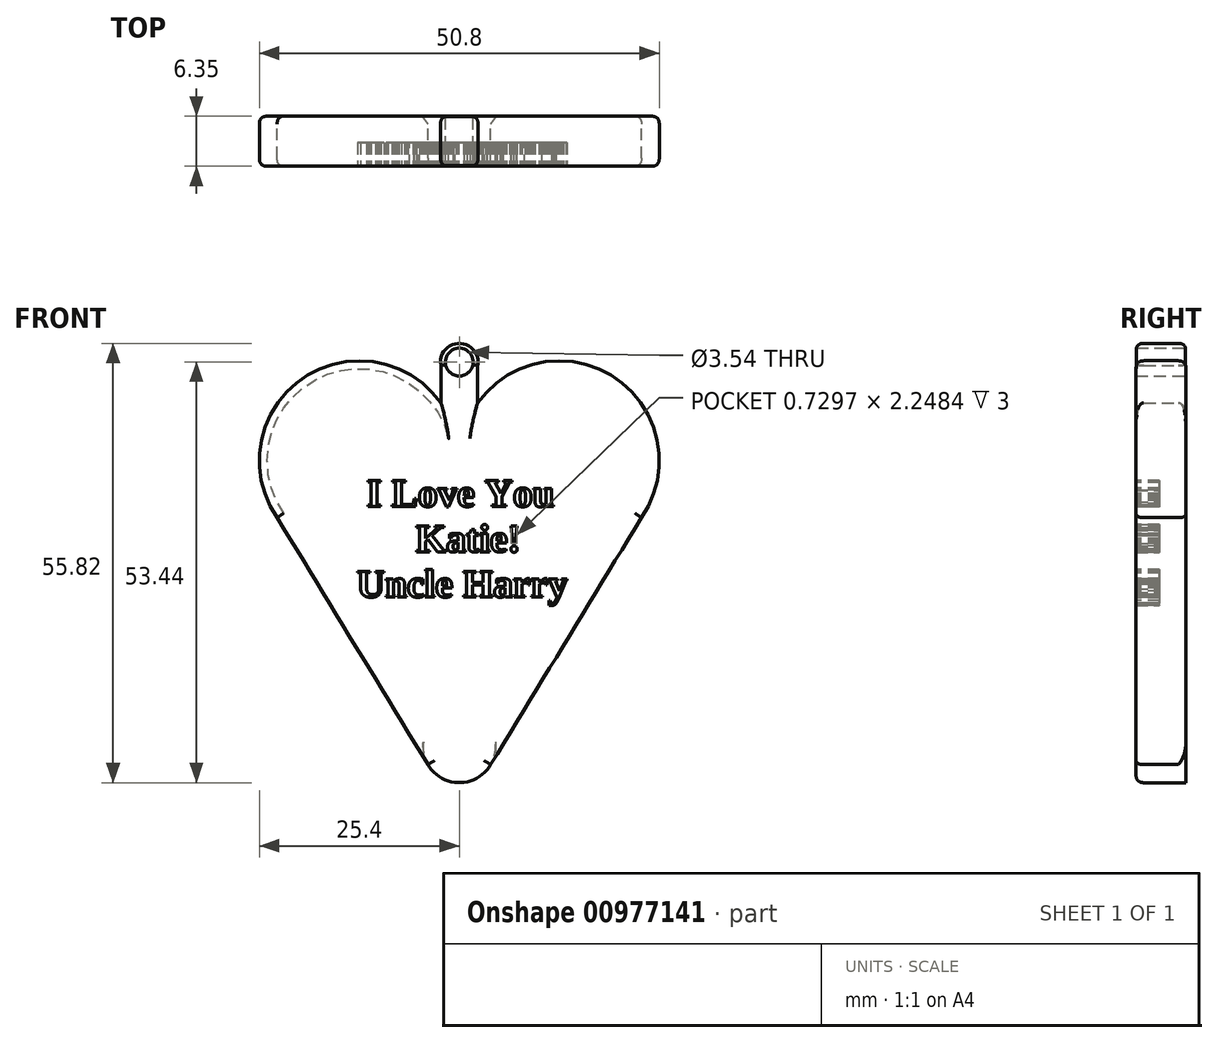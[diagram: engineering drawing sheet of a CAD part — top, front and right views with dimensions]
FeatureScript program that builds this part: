
annotation { "Feature Type Name" : "Feature", "Feature Type Description" : "" }
export const myFeature = defineFeature(function(context is Context, id is Id, definition is map)
    precondition{}
    {
        {
            var Q0;
            Q0=qCreatedBy(makeId("Front.planeOp"),FACE);
            var sketch = newSketch(context, id + "F0", { "sketchPlane" : qUnion([Q0])});
            skCircle(sketch, "E0", {"center": v(-12.7, -40.15) * mm, "radius": 12.7 * mm});
            skCircle(sketch, "E1", {"center": v(12.7, -40.15) * mm, "radius": 12.7 * mm});
            skCircle(sketch, "E2", {"center": v(0, -76.44) * mm, "radius": 4.6 * mm});
            skCircle(sketch, "E3", {"center": v(0, -27.61) * mm, "radius": 2.38 * mm});
            skLineSegment(sketch, "E4", {"start": v(-2.34, -28.04) * mm, "end": v(-2.34, -32.8) * mm});
            skLineSegment(sketch, "E5", {"start": v(-2.34, -32.8) * mm, "end": v(2.34, -32.8) * mm});
            skLineSegment(sketch, "E6", {"start": v(2.34, -32.8) * mm, "end": v(2.34, -28.04) * mm});
            skLineSegment(sketch, "E7", {"start": v(23.9, -46.13) * mm, "end": v(4, -78.74) * mm});
            skLineSegment(sketch, "E8", {"start": v(-23.9, -46.13) * mm, "end": v(-4, -78.74) * mm});
            skCircle(sketch, "E9", {"center": v(0, -27.61) * mm, "radius": 1.77 * mm});
            skSolve(sketch);
        }
        {
            var Q0;
            {var subQ0=sQuery(id+"F0.wireOp",EDGE,"c1dc9967-65be-475e-a1ab-9509db93362e");var subQ1=sQuery(id+"F0.wireOp",EDGE,"E0");var subQ2=makeQuery(id+"F0.imprint","INTERSECT",VERTEX,{"disambiguationData":[OD(0.0)],"derivedFrom":[subQ1,subQ0]});Q0=makeQuery(id+"F0.imprint","IMPRINT",FACE,{"disambiguationData":[TD([[makeQuery(id+"F0.imprint","IMPRINT",EDGE,{"disambiguationData":[TD([[subQ2,1.0]])],"derivedFrom":subQ1}),1.0]])]});}
            var Q1;
            {var subQ3=sQuery(id+"F0.wireOp",EDGE,"E1");var subQ5=sQuery(id+"F0.wireOp",EDGE,"E0");var subQ6=makeQuery(id+"F0.imprint","INTERSECT",VERTEX,{"derivedFrom":[subQ5,subQ3]});Q1=makeQuery(id+"F0.imprint","IMPRINT",FACE,{"disambiguationData":[TD([[makeQuery(id+"F0.imprint","IMPRINT",EDGE,{"disambiguationData":[TD([[subQ6,1.0]])],"derivedFrom":subQ5}),-1.0]])]});}
            var Q2;
            {var subQ0=sQuery(id+"F0.wireOp",EDGE,"E1");var subQ1=makeQuery(id+"F0.imprint","INTERSECT",VERTEX,{"derivedFrom":[sQuery(id+"F0.wireOp",EDGE,"E0"),subQ0]});Q2=makeQuery(id+"F0.imprint","IMPRINT",FACE,{"disambiguationData":[TD([[makeQuery(id+"F0.imprint","IMPRINT",EDGE,{"disambiguationData":[TD([[subQ1,-1.0]])],"derivedFrom":subQ0}),1.0]])]});}
            var Q3;
            {var subQ0=sQuery(id+"F0.wireOp",EDGE,"E2");var subQ1=makeQuery(id+"F0.imprint","INTERSECT",VERTEX,{"derivedFrom":[subQ0,sQuery(id+"F0.wireOp",EDGE,"22bdcb90-6837-4773-9a82-ad14b141443f")]});Q3=makeQuery(id+"F0.imprint","IMPRINT",FACE,{"disambiguationData":[TD([[makeQuery(id+"F0.imprint","IMPRINT",EDGE,{"disambiguationData":[TD([[subQ1,1.0]])],"derivedFrom":subQ0}),1.0]])]});}
            var Q4;
            {var subQ3=sQuery(id+"F0.wireOp",EDGE,"d9c96f0d-c952-4023-af67-c3b31cf93496");Q4=makeQuery(id+"F0.imprint","IMPRINT",FACE,{"disambiguationData":[TD([[makeQuery(id+"F0.imprint","IMPRINT",EDGE,{"derivedFrom":subQ3}),1.0]])]});}
            var Q5;
            {var subQ0=sQuery(id+"F0.wireOp",EDGE,"43af675b-4bb7-419d-b6aa-33dcd8a345be");Q5=makeQuery(id+"F0.imprint","IMPRINT",FACE,{"disambiguationData":[TD([[makeQuery(id+"F0.imprint","IMPRINT",EDGE,{"derivedFrom":subQ0}),1.0]])]});}
            extrude(context, id + "F1", {"entities" : qUnion([Q0, Q1, Q2, Q3, Q4, Q5]), "depth" : 1 / 203.2 * mm});
        }
        {
            var Q0;
            Q0=qSketchRegion(id+"F0",true);
            var Q1;
            Q1=makeQuery(id+"F0.imprint","IMPRINT",FACE,{"disambiguationData":[TD([[makeQuery(id+"F0.imprint","IMPRINT",EDGE,{"derivedFrom":sQuery(id+"F0.wireOp",EDGE,"E3")}),-1.0]])]});
            extrude(context, id + "F2", {"entities" : qUnion([Q0, Q1]), "operationType" : NewBodyOperationType.ADD, "depth" : 6.35 * mm});
        }
        {
            var Q0;
            {var subQ0=sQuery(id+"F0.wireOp",EDGE,"E1");Q0=makeQuery(id+"F2.boolean.opBoolean","MERGE",EDGE,{"derivedFrom":[makeQuery(id+"F1.opExtrude","CAP_EDGE",EDGE,{"disambiguationData":[OSD([subQ0])],"isStart":false}),makeQuery(id+"F2.opExtrude","CAP_EDGE",EDGE,{"disambiguationData":[OSD([subQ0])],"isStart":false})]});}
            var Q1;
            Q1=makeQuery(id+"F1.opExtrude","CAP_EDGE",EDGE,{"disambiguationData":[OSD([sQuery(id+"F0.wireOp",EDGE,"E7")])],"isStart":false});
            var Q2;
            Q2=makeQuery(id+"F2.opExtrude","CAP_EDGE",EDGE,{"disambiguationData":[OSD([sQuery(id+"F0.wireOp",EDGE,"E0")])],"isStart":false});
            var Q3;
            Q3=makeQuery(id+"F1.opExtrude","CAP_EDGE",EDGE,{"disambiguationData":[OSD([sQuery(id+"F0.wireOp",EDGE,"E8")])],"isStart":false});
            var Q4;
            Q4=makeQuery(id+"F2.opExtrude","CAP_EDGE",EDGE,{"disambiguationData":[OSD([sQuery(id+"F0.wireOp",EDGE,"E2")])],"isStart":false});
            var Q5;
            {var subQ0=sQuery(id+"F0.wireOp",EDGE,"E1");Q5=makeQuery(id+"F2.boolean.opBoolean","MERGE",EDGE,{"derivedFrom":[makeQuery(id+"F1.opExtrude","CAP_EDGE",EDGE,{"disambiguationData":[OSD([subQ0])],"isStart":true}),makeQuery(id+"F2.opExtrude","CAP_EDGE",EDGE,{"disambiguationData":[OSD([subQ0])],"isStart":true})]});}
            var Q6;
            Q6=makeQuery(id+"F1.opExtrude","CAP_EDGE",EDGE,{"disambiguationData":[OSD([sQuery(id+"F0.wireOp",EDGE,"E7")])],"isStart":true});
            var Q7;
            Q7=makeQuery(id+"F2.opExtrude","CAP_EDGE",EDGE,{"disambiguationData":[OSD([sQuery(id+"F0.wireOp",EDGE,"E2")])],"isStart":true});
            var Q8;
            Q8=makeQuery(id+"F1.opExtrude","CAP_EDGE",EDGE,{"disambiguationData":[OSD([sQuery(id+"F0.wireOp",EDGE,"E8")])],"isStart":true});
            var Q9;
            Q9=makeQuery(id+"F2.opExtrude","CAP_EDGE",EDGE,{"disambiguationData":[OSD([sQuery(id+"F0.wireOp",EDGE,"E0")])],"isStart":true});
            var Q10;
            Q10=makeQuery(id+"F2.opExtrude","CAP_EDGE",EDGE,{"disambiguationData":[OSD([sQuery(id+"F0.wireOp",EDGE,"E6")])],"isStart":true});
            var Q11;
            Q11=makeQuery(id+"F2.opExtrude","CAP_EDGE",EDGE,{"disambiguationData":[OSD([sQuery(id+"F0.wireOp",EDGE,"E4")])],"isStart":true});
            var Q12;
            Q12=makeQuery(id+"F2.opExtrude","CAP_EDGE",EDGE,{"disambiguationData":[OSD([sQuery(id+"F0.wireOp",EDGE,"E3")])],"isStart":true});
            var Q13;
            Q13=makeQuery(id+"F2.opExtrude","CAP_EDGE",EDGE,{"disambiguationData":[OSD([sQuery(id+"F0.wireOp",EDGE,"E4")])],"isStart":false});
            var Q14;
            Q14=makeQuery(id+"F2.opExtrude","CAP_EDGE",EDGE,{"disambiguationData":[OSD([sQuery(id+"F0.wireOp",EDGE,"E3")])],"isStart":false});
            var Q15;
            Q15=makeQuery(id+"F2.opExtrude","CAP_EDGE",EDGE,{"disambiguationData":[OSD([sQuery(id+"F0.wireOp",EDGE,"E6")])],"isStart":false});
            var Q16;
            Q16=makeQuery(id+"F2.opExtrude","CAP_EDGE",EDGE,{"disambiguationData":[OSD([sQuery(id+"F0.wireOp",EDGE,"E1")])],"isStart":false});
            fillet(context, id + "F3", {"entities" : qUnion([Q0, Q1, Q2, Q3, Q4, Q5, Q6, Q7, Q8, Q9, Q10, Q11, Q12, Q13, Q14, Q15, Q16]), "radius" : 1 * mm, "tangentPropagation" : true, "rho" : .5, "crossSection" : FilletCrossSection.CONIC, "allowEdgeOverflow" : false});
        }
        {
            var Q0;
            Q0=makeQuery(id+"F2.opExtrude","CAP_FACE",FACE,{"disambiguationData":[OSD([sQuery(id+"F0.wireOp",EDGE,"E0"),sQuery(id+"F0.wireOp",EDGE,"E1"),sQuery(id+"F0.wireOp",EDGE,"E2"),sQuery(id+"F0.wireOp",EDGE,"E4"),sQuery(id+"F0.wireOp",EDGE,"E6"),sQuery(id+"F0.wireOp",EDGE,"E3"),sQuery(id+"F0.wireOp",EDGE,"E7"),sQuery(id+"F0.wireOp",EDGE,"E8"),sQuery(id+"F0.wireOp",EDGE,"E9")])],"isStart":false});
            var sketch = newSketch(context, id + "F4", { "sketchPlane" : qUnion([Q0])});
            skText(sketch, "E10", { "text": " I Love You\n      Katie!\nUncle Harry", "fontName": "Tinos-Bold.ttf"});
            const initialGuessF4  = {"E10": [-0.01304, -0.04596, 1, 0, 0.0036]};
            skSetInitialGuess(sketch, initialGuessF4);
            skSolve(sketch);
        }
        {
            var Q0;
            Q0=qSketchRegion(id+"F4",true);
            extrude(context, id + "F5", {"entities" : qUnion([Q0]), "operationType" : NewBodyOperationType.REMOVE, "oppositeDirection" : true, "depth" : 3 * mm, "offsetDistance" : 25 * mm});
        }
    });
